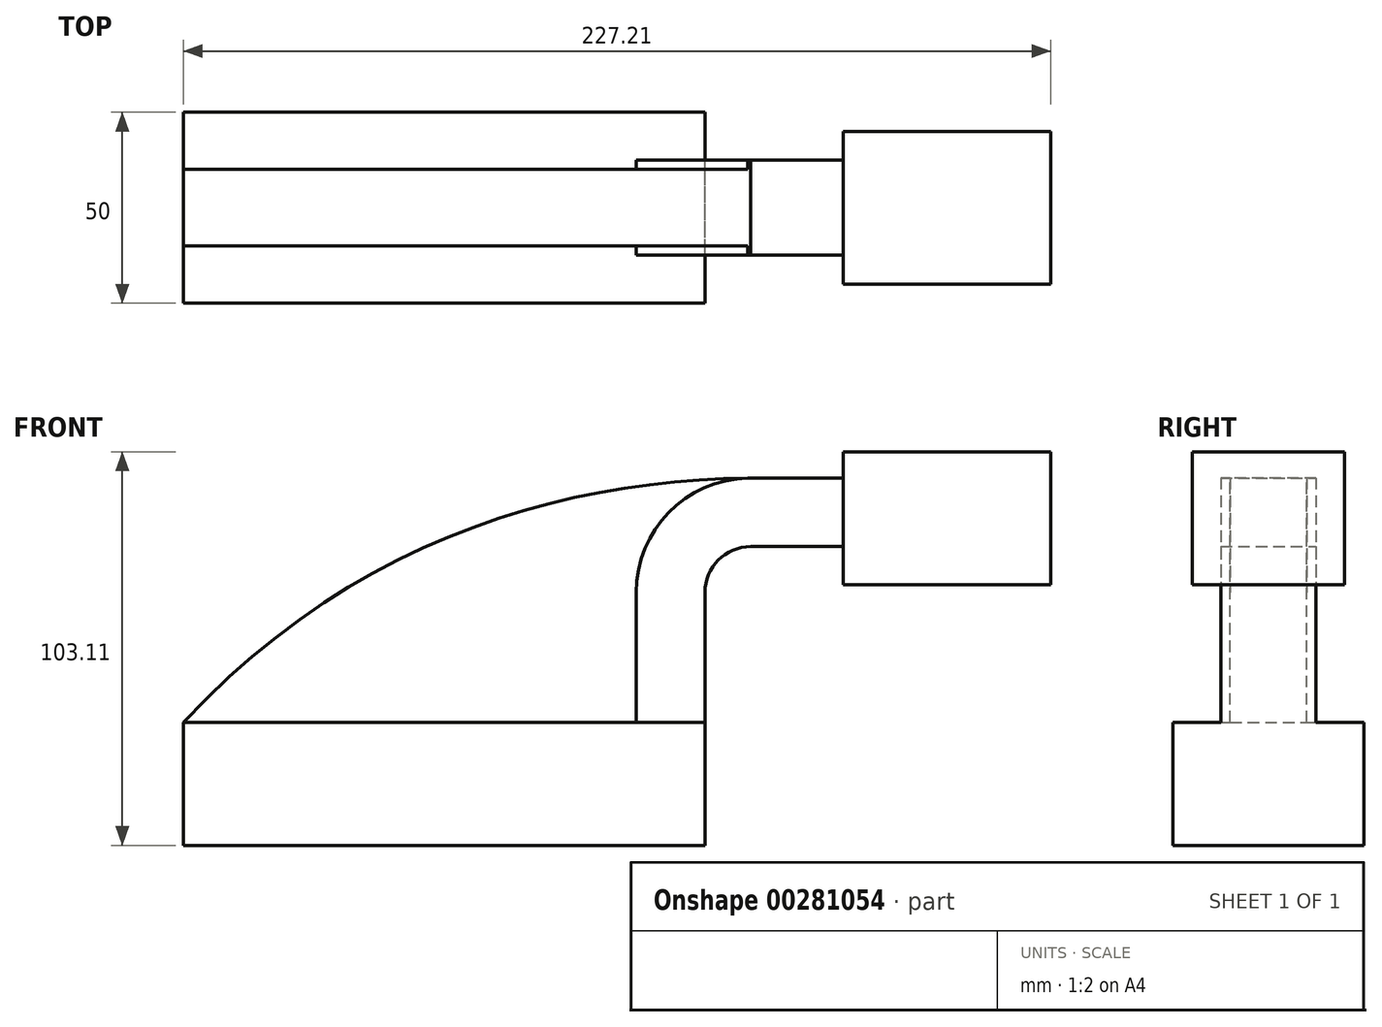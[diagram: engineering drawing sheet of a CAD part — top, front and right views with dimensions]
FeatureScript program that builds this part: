
annotation { "Feature Type Name" : "Feature", "Feature Type Description" : "" }
export const myFeature = defineFeature(function(context is Context, id is Id, definition is map)
    precondition{}
    {
        {
            var Q0;
            Q0=qCreatedBy(makeId("Front.planeOp"),FACE);
            var sketch = newSketch(context, id + "F0", { "sketchPlane" : qUnion([Q0])});
            skLineSegment(sketch, "E0.bottom", {"start": v(0, -9.63) * mm, "end": v(-136.6, -9.63) * mm});
            skLineSegment(sketch, "E0.top", {"start": v(0, -41.92) * mm, "end": v(-136.6, -41.92) * mm});
            skLineSegment(sketch, "E0.left", {"start": v(0, -9.63) * mm, "end": v(0, -41.92) * mm});
            skLineSegment(sketch, "E0.right", {"start": v(-136.6, -9.63) * mm, "end": v(-136.6, -41.92) * mm});
            skPoint(sketch, "E0.middle", {"position": v(-68.3, -25.78) * mm});
            skLineSegment(sketch, "E1.bottom", {"start": v(90.61, 61.19) * mm, "end": v(36.23, 61.19) * mm});
            skLineSegment(sketch, "E1.top", {"start": v(90.61, 26.34) * mm, "end": v(36.23, 26.34) * mm});
            skLineSegment(sketch, "E1.left", {"start": v(90.61, 61.19) * mm, "end": v(90.61, 26.34) * mm});
            skLineSegment(sketch, "E1.right", {"start": v(36.23, 61.19) * mm, "end": v(36.23, 26.34) * mm});
            skPoint(sketch, "E1.middle", {"position": v(63.42, 43.77) * mm});
            skLineSegment(sketch, "E2", {"start": v(0, -9.63) * mm, "end": v(0, 24.36) * mm});
            skArc(sketch, "E3", {"start": v(0, 24.36) * mm, "mid": v(3.51, 32.85) * mm, "end": v(12, 36.36) * mm});
            skLineSegment(sketch, "E4", {"start": v(12, 36.36) * mm, "end": v(50.5, 36.36) * mm});
            skLineSegment(sketch, "E5.0", {"start": v(12, 54.36) * mm, "end": v(50.5, 54.36) * mm});
            skArc(sketch, "E5.1", {"start": v(-18, 24.36) * mm, "mid": v(-9.21, 45.57) * mm, "end": v(12, 54.36) * mm});
            skLineSegment(sketch, "E5.2", {"start": v(-18, -9.63) * mm, "end": v(-18, 24.36) * mm});
            skFitSpline(sketch, "E6", {"points": [v(-136.6, -9.63) * mm, v(12, 54.36) * mm], "startDerivative": vector(135.19, 145.32) * mm, "endDerivative": vector(145.74, 1.62) * mm});
            skSolve(sketch);
        }
        {
            var Q0;
            Q0=makeQuery(id+"F0.imprint","IMPRINT",FACE,{"disambiguationData":[TD([[makeQuery(id+"F0.imprint","IMPRINT",EDGE,{"derivedFrom":sQuery(id+"F0.wireOp",EDGE,"E0.top")}),-1.0]])]});
            extrude(context, id + "F1", {"entities" : qUnion([Q0]), "endBound" : BoundingType.SYMMETRIC, "depth" : 50 * mm});
        }
        {
            var Q0;
            {var subQ3=sQuery(id+"F0.wireOp",EDGE,"E5.2");Q0=makeQuery(id+"F0.imprint","IMPRINT",FACE,{"disambiguationData":[TD([[makeQuery(id+"F0.imprint","IMPRINT",EDGE,{"derivedFrom":subQ3}),1.0]])]});}
            extrude(context, id + "F2", {"entities" : qUnion([Q0]), "operationType" : NewBodyOperationType.ADD, "endBound" : BoundingType.SYMMETRIC, "depth" : 20 * mm});
        }
        {
            var Q0;
            {var subQ1=sQuery(id+"F0.wireOp",EDGE,"E2");Q0=makeQuery(id+"F0.imprint","IMPRINT",FACE,{"disambiguationData":[TD([[makeQuery(id+"F0.imprint","IMPRINT",EDGE,{"derivedFrom":subQ1}),1.0]])]});}
            extrude(context, id + "F3", {"entities" : qUnion([Q0]), "operationType" : NewBodyOperationType.ADD, "endBound" : BoundingType.SYMMETRIC, "depth" : 25 * mm});
        }
        {
            var Q0;
            {var subQ1=sQuery(id+"F0.wireOp",EDGE,"E1.bottom");Q0=makeQuery(id+"F0.imprint","IMPRINT",FACE,{"disambiguationData":[TD([[makeQuery(id+"F0.imprint","IMPRINT",EDGE,{"derivedFrom":subQ1}),1.0]])]});}
            extrude(context, id + "F4", {"entities" : qUnion([Q0]), "operationType" : NewBodyOperationType.ADD, "endBound" : BoundingType.SYMMETRIC, "depth" : 40 * mm});
        }
    });
